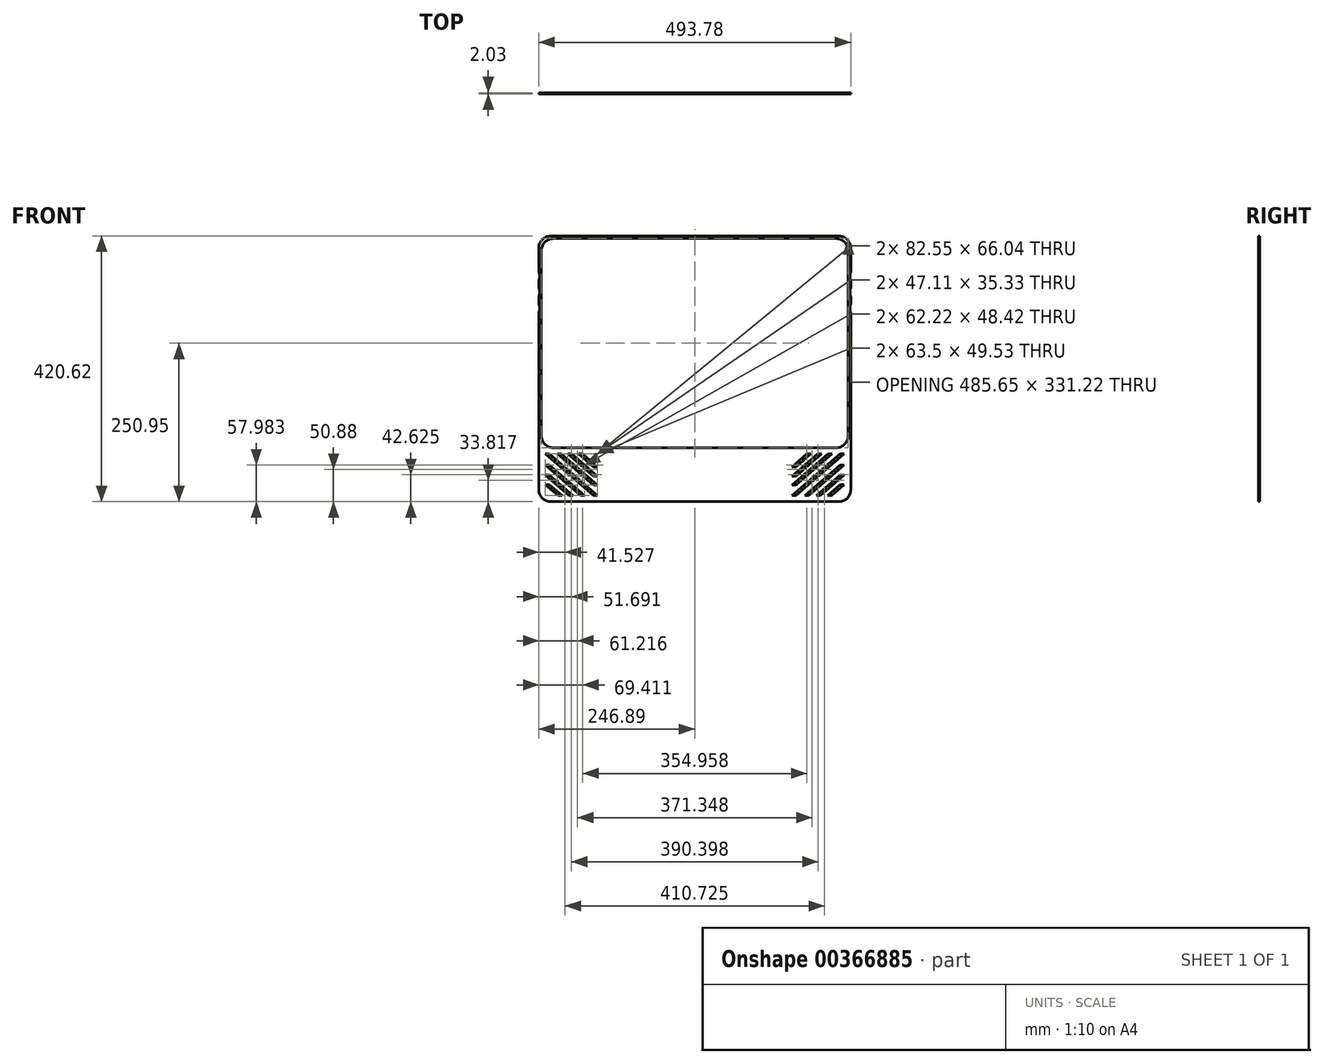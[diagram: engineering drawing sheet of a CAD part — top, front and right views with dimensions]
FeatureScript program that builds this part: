
annotation { "Feature Type Name" : "Feature", "Feature Type Description" : "" }
export const myFeature = defineFeature(function(context is Context, id is Id, definition is map)
    precondition{}
    {
        {
            var Q0;
            Q0=qCreatedBy(makeId("Front.planeOp"),FACE);
            var sketch = newSketch(context, id + "F0", { "sketchPlane" : qUnion([Q0])});
            skLineSegment(sketch, "E0.bottom", {"start": v(227.84, 210.31) * mm, "end": v(-227.84, 210.31) * mm});
            skLineSegment(sketch, "E0.top", {"start": v(227.84, -210.31) * mm, "end": v(-227.84, -210.31) * mm});
            skLineSegment(sketch, "E0.left", {"start": v(246.89, 191.26) * mm, "end": v(246.89, -191.26) * mm});
            skLineSegment(sketch, "E0.right", {"start": v(-246.89, 191.26) * mm, "end": v(-246.89, -191.26) * mm});
            skPoint(sketch, "E0.middle", {"position": v(0, 0) * mm});
            skPoint(sketch, "E1.visualSharp", {"position": v(-246.89, 210.31) * mm});
            skArc(sketch, "E1.filletArc", {"start": v(-227.84, 210.31) * mm, "mid": v(-241.3, 204.73) * mm, "end": v(-246.89, 191.26) * mm});
            skPoint(sketch, "E2.visualSharp", {"position": v(246.89, 210.31) * mm});
            skArc(sketch, "E2.filletArc", {"start": v(246.89, 191.26) * mm, "mid": v(241.3, 204.73) * mm, "end": v(227.84, 210.31) * mm});
            skPoint(sketch, "E3.visualSharp", {"position": v(246.89, -210.31) * mm});
            skArc(sketch, "E3.filletArc", {"start": v(227.84, -210.31) * mm, "mid": v(241.3, -204.73) * mm, "end": v(246.89, -191.26) * mm});
            skPoint(sketch, "E4.visualSharp", {"position": v(-246.89, -210.31) * mm});
            skArc(sketch, "E4.filletArc", {"start": v(-246.89, -191.26) * mm, "mid": v(-241.3, -204.73) * mm, "end": v(-227.84, -210.31) * mm});
            skSolve(sketch);
        }
        {
            var Q0;
            Q0=qCreatedBy(makeId("Front.planeOp"),FACE);
            var sketch = newSketch(context, id + "F1", { "sketchPlane" : qUnion([Q0])});
            skLineSegment(sketch, "E5.bottom", {"start": v(-223.77, 206.25) * mm, "end": v(223.77, 206.25) * mm});
            skLineSegment(sketch, "E5.top", {"start": v(-223.77, -124.97) * mm, "end": v(223.77, -124.97) * mm});
            skLineSegment(sketch, "E5.left", {"start": v(-242.82, 187.2) * mm, "end": v(-242.82, -105.92) * mm});
            skLineSegment(sketch, "E5.right", {"start": v(242.82, 187.2) * mm, "end": v(242.82, -105.92) * mm});
            skPoint(sketch, "E6.visualSharp", {"position": v(-242.82, 206.25) * mm});
            skArc(sketch, "E6.filletArc", {"start": v(-223.77, 206.25) * mm, "mid": v(-237.24, 200.67) * mm, "end": v(-242.82, 187.2) * mm});
            skPoint(sketch, "E7.visualSharp", {"position": v(242.82, 206.25) * mm});
            skArc(sketch, "E7.filletArc", {"start": v(242.82, 187.2) * mm, "mid": v(237.24, 200.67) * mm, "end": v(223.77, 206.25) * mm});
            skPoint(sketch, "E8.visualSharp", {"position": v(242.82, -124.97) * mm});
            skArc(sketch, "E8.filletArc", {"start": v(223.77, -124.97) * mm, "mid": v(237.24, -119.39) * mm, "end": v(242.82, -105.92) * mm});
            skPoint(sketch, "E9.visualSharp", {"position": v(-242.82, -124.97) * mm});
            skArc(sketch, "E9.filletArc", {"start": v(-242.82, -105.92) * mm, "mid": v(-237.24, -119.39) * mm, "end": v(-223.77, -124.97) * mm});
            skSolve(sketch);
        }
        {
            var Q0;
            Q0 = qSketchRegion(id + "F0", true);
            extrude(context, id + "F2", {"entities" : qUnion([Q0]), "depth" : 2.03 * mm});
        }
        {
            var Q0;
            Q0 = qSketchRegion(id + "F1", true);
            extrude(context, id + "F3", {"entities" : qUnion([Q0]), "operationType" : NewBodyOperationType.REMOVE, "depth" : 2.54 * mm});
        }
        {
            var Q0;
            Q0=qCreatedBy(makeId("Front.planeOp"),FACE);
            var sketch = newSketch(context, id + "F4", { "sketchPlane" : qUnion([Q0])});
            skLineSegment(sketch, "E10", {"start": v(-236.47, -134.66) * mm, "end": v(-230.12, -134.66) * mm});
            skLineSegment(sketch, "E11", {"start": v(-230.12, -134.66) * mm, "end": v(-153.92, -200.7) * mm});
            skLineSegment(sketch, "E12", {"start": v(-153.92, -200.7) * mm, "end": v(-160.27, -200.7) * mm});
            skLineSegment(sketch, "E13", {"start": v(-160.27, -200.7) * mm, "end": v(-236.47, -134.66) * mm});
            skLineSegment(sketch, "E14", {"start": v(-217.42, -134.66) * mm, "end": v(-211.07, -134.66) * mm});
            skPoint(sketch, "E15.endSnap0", {"position": v(-157.1, -200.7) * mm});
            skLineSegment(sketch, "E16", {"start": v(-153.92, -184.2) * mm, "end": v(-160.27, -184.2) * mm});
            skLineSegment(sketch, "E17", {"start": v(-160.27, -184.2) * mm, "end": v(-217.42, -134.66) * mm});
            skLineSegment(sketch, "E18", {"start": v(-211.07, -134.66) * mm, "end": v(-153.92, -184.2) * mm});
            skLineSegment(sketch, "E19", {"start": v(-236.47, -152.28) * mm, "end": v(-230.12, -152.28) * mm});
            skLineSegment(sketch, "E20", {"start": v(-230.12, -152.28) * mm, "end": v(-174.25, -200.7) * mm});
            skLineSegment(sketch, "E21", {"start": v(-174.25, -200.7) * mm, "end": v(-180.6, -200.7) * mm});
            skLineSegment(sketch, "E22", {"start": v(-180.6, -200.7) * mm, "end": v(-236.47, -152.28) * mm});
            skLineSegment(sketch, "E23", {"start": v(-236.47, -168.23) * mm, "end": v(-230.12, -168.23) * mm});
            skLineSegment(sketch, "E24", {"start": v(-230.12, -168.23) * mm, "end": v(-192.65, -200.7) * mm});
            skLineSegment(sketch, "E25", {"start": v(-192.65, -200.7) * mm, "end": v(-199, -200.7) * mm});
            skLineSegment(sketch, "E26", {"start": v(-199, -200.7) * mm, "end": v(-236.47, -168.23) * mm});
            skLineSegment(sketch, "E27", {"start": v(-236.47, -183.4) * mm, "end": v(-230.12, -183.4) * mm});
            skLineSegment(sketch, "E28", {"start": v(-230.12, -183.4) * mm, "end": v(-210.16, -200.7) * mm});
            skLineSegment(sketch, "E29", {"start": v(-210.16, -200.7) * mm, "end": v(-216.5, -200.7) * mm});
            skLineSegment(sketch, "E30", {"start": v(-216.5, -200.7) * mm, "end": v(-236.47, -183.4) * mm});
            skLineSegment(sketch, "E31", {"start": v(-153.92, -170) * mm, "end": v(-160.27, -170) * mm});
            skLineSegment(sketch, "E32", {"start": v(-160.27, -170) * mm, "end": v(-201.03, -134.66) * mm});
            skLineSegment(sketch, "E33", {"start": v(-201.03, -134.66) * mm, "end": v(-194.68, -134.66) * mm});
            skLineSegment(sketch, "E34", {"start": v(-194.68, -134.66) * mm, "end": v(-153.92, -170) * mm});
            skLineSegment(sketch, "E35", {"start": v(-153.92, -155.14) * mm, "end": v(-160.27, -155.14) * mm});
            skLineSegment(sketch, "E36", {"start": v(-160.27, -155.14) * mm, "end": v(-183.9, -134.66) * mm});
            skLineSegment(sketch, "E37", {"start": v(-183.9, -134.66) * mm, "end": v(-177.55, -134.66) * mm});
            skLineSegment(sketch, "E38", {"start": v(-177.55, -134.66) * mm, "end": v(-153.92, -155.14) * mm});
            skLineSegment(sketch, "E39.MirrorCS", {"start": v(217.42, -134.66) * mm, "end": v(211.07, -134.66) * mm});
            skLineSegment(sketch, "E40.MirrorCS", {"start": v(236.47, -134.66) * mm, "end": v(230.12, -134.66) * mm});
            skLineSegment(sketch, "E41.MirrorCS", {"start": v(201.03, -134.66) * mm, "end": v(194.68, -134.66) * mm});
            skLineSegment(sketch, "E42.MirrorCS", {"start": v(153.92, -155.14) * mm, "end": v(160.27, -155.14) * mm});
            skLineSegment(sketch, "E43.MirrorCS", {"start": v(183.9, -134.66) * mm, "end": v(177.55, -134.66) * mm});
            skLineSegment(sketch, "E44.MirrorCS", {"start": v(236.47, -168.23) * mm, "end": v(230.12, -168.23) * mm});
            skLineSegment(sketch, "E45.MirrorCS", {"start": v(174.25, -200.7) * mm, "end": v(180.6, -200.7) * mm});
            skLineSegment(sketch, "E46.MirrorCS", {"start": v(153.92, -184.2) * mm, "end": v(160.27, -184.2) * mm});
            skLineSegment(sketch, "E47.MirrorCS", {"start": v(153.92, -200.7) * mm, "end": v(160.27, -200.7) * mm});
            skLineSegment(sketch, "E48.MirrorCS", {"start": v(210.16, -200.7) * mm, "end": v(216.5, -200.7) * mm});
            skLineSegment(sketch, "E49.MirrorCS", {"start": v(153.92, -170) * mm, "end": v(160.27, -170) * mm});
            skLineSegment(sketch, "E50.MirrorCS", {"start": v(236.47, -183.4) * mm, "end": v(230.12, -183.4) * mm});
            skLineSegment(sketch, "E51.MirrorCS", {"start": v(236.47, -152.28) * mm, "end": v(230.12, -152.28) * mm});
            skLineSegment(sketch, "E52.MirrorCS", {"start": v(192.65, -200.7) * mm, "end": v(199, -200.7) * mm});
            skLineSegment(sketch, "E53.MirrorCS", {"start": v(230.12, -183.4) * mm, "end": v(210.16, -200.7) * mm});
            skLineSegment(sketch, "E54.MirrorCS", {"start": v(160.27, -200.7) * mm, "end": v(236.47, -134.66) * mm});
            skLineSegment(sketch, "E55.MirrorCS", {"start": v(194.68, -134.66) * mm, "end": v(153.92, -170) * mm});
            skLineSegment(sketch, "E56.MirrorCS", {"start": v(230.12, -134.66) * mm, "end": v(153.92, -200.7) * mm});
            skLineSegment(sketch, "E57.MirrorCS", {"start": v(199, -200.7) * mm, "end": v(236.47, -168.23) * mm});
            skLineSegment(sketch, "E58.MirrorCS", {"start": v(230.12, -168.23) * mm, "end": v(192.65, -200.7) * mm});
            skLineSegment(sketch, "E59.MirrorCS", {"start": v(160.27, -155.14) * mm, "end": v(183.9, -134.66) * mm});
            skLineSegment(sketch, "E60.MirrorCS", {"start": v(216.5, -200.7) * mm, "end": v(236.47, -183.4) * mm});
            skLineSegment(sketch, "E61.MirrorCS", {"start": v(160.27, -184.2) * mm, "end": v(217.42, -134.66) * mm});
            skLineSegment(sketch, "E62.MirrorCS", {"start": v(177.55, -134.66) * mm, "end": v(153.92, -155.14) * mm});
            skPoint(sketch, "E63.MirrorP", {"position": v(157.1, -200.7) * mm});
            skLineSegment(sketch, "E64.MirrorCS", {"start": v(180.6, -200.7) * mm, "end": v(236.47, -152.28) * mm});
            skLineSegment(sketch, "E65.MirrorCS", {"start": v(160.27, -170) * mm, "end": v(201.03, -134.66) * mm});
            skLineSegment(sketch, "E66.MirrorCS", {"start": v(230.12, -152.28) * mm, "end": v(174.25, -200.7) * mm});
            skLineSegment(sketch, "E67.MirrorCS", {"start": v(211.07, -134.66) * mm, "end": v(153.92, -184.2) * mm});
            skSolve(sketch);
        }
        {
            var Q0;
            Q0 = qSketchRegion(id + "F4", true);
            extrude(context, id + "F5", {"entities" : qUnion([Q0]), "operationType" : NewBodyOperationType.REMOVE, "depth" : 25.4 * mm});
        }
        {
            var Q0;
            Q0=qCreatedBy(makeId("Front.planeOp"),FACE);
            var sketch = newSketch(context, id + "F6", { "sketchPlane" : qUnion([Q0])});
            skCircle(sketch, "E68", {"center": v(264.67, 146.81) * mm, "radius": 19.05 * mm});
            skCircle(sketch, "E69", {"center": v(264.67, 121.41) * mm, "radius": 19.05 * mm});
            skCircle(sketch, "E70", {"center": v(264.67, 96.01) * mm, "radius": 19.05 * mm});
            skCircle(sketch, "E71", {"center": v(-264.67, 146.81) * mm, "radius": 19.05 * mm});
            skCircle(sketch, "E72", {"center": v(-264.67, 121.41) * mm, "radius": 19.05 * mm});
            skCircle(sketch, "E73", {"center": v(-264.67, 96.01) * mm, "radius": 19.05 * mm});
            skSolve(sketch);
        }
        {
            var Q0;
            Q0 = qSketchRegion(id + "F6", true);
            extrude(context, id + "F7", {"entities" : qUnion([Q0]), "operationType" : NewBodyOperationType.REMOVE, "depth" : 25.4 * mm});
        }
    });
